# Revit family: TD92_VAN053_PRE009_RVT20_R00
name_source: partatom
category: Mobiliário
units: mm (PartAtom-declared; Revit-internal decimal feet)

## family parameters
Com base no plano de trabalho = Não
Compartilhado = Não
Corte com vazios quando carregada = Não
Número OmniClass = 23.40.20.00
Ponto de cálculo do ambiente = Não
Sempre na vertical = Sim
Título OmniClass = General Furniture and Specialties

## types (1)
- TD92_VAN053_PRE009_RVT20_R00
    Descrição = Clean, prática e confortável, a linha de cadeira Vanda é adaptável para diferentes lugares. Com um design pensado na postura, a linha Vanda tem o encosto mais alto, acomoda melhor e garante uma posição aconchegante. A Cadeira Tramontina Vanda em Polipropileno com Pernas Anodizadas é leve, resistente e com design diferenciado. Submetida a rigorosos testes de qualidade, a cadeira resiste a uma carga estática de até 154 kg.
    Elevação padrão = 0  [stored 0 ft]
    Fabricante = Tramontina Delta S/A
    Modelo = Cadeira Tramontina Vanda em Polipropileno com Pernas Anodizadas Preto
    Nota-chave = 92053009
    URL = https://www.tramontinastore.com

note: [stored X ft] marks values corroborated as IEEE doubles in the binary element streams (Revit-internal decimal feet)
